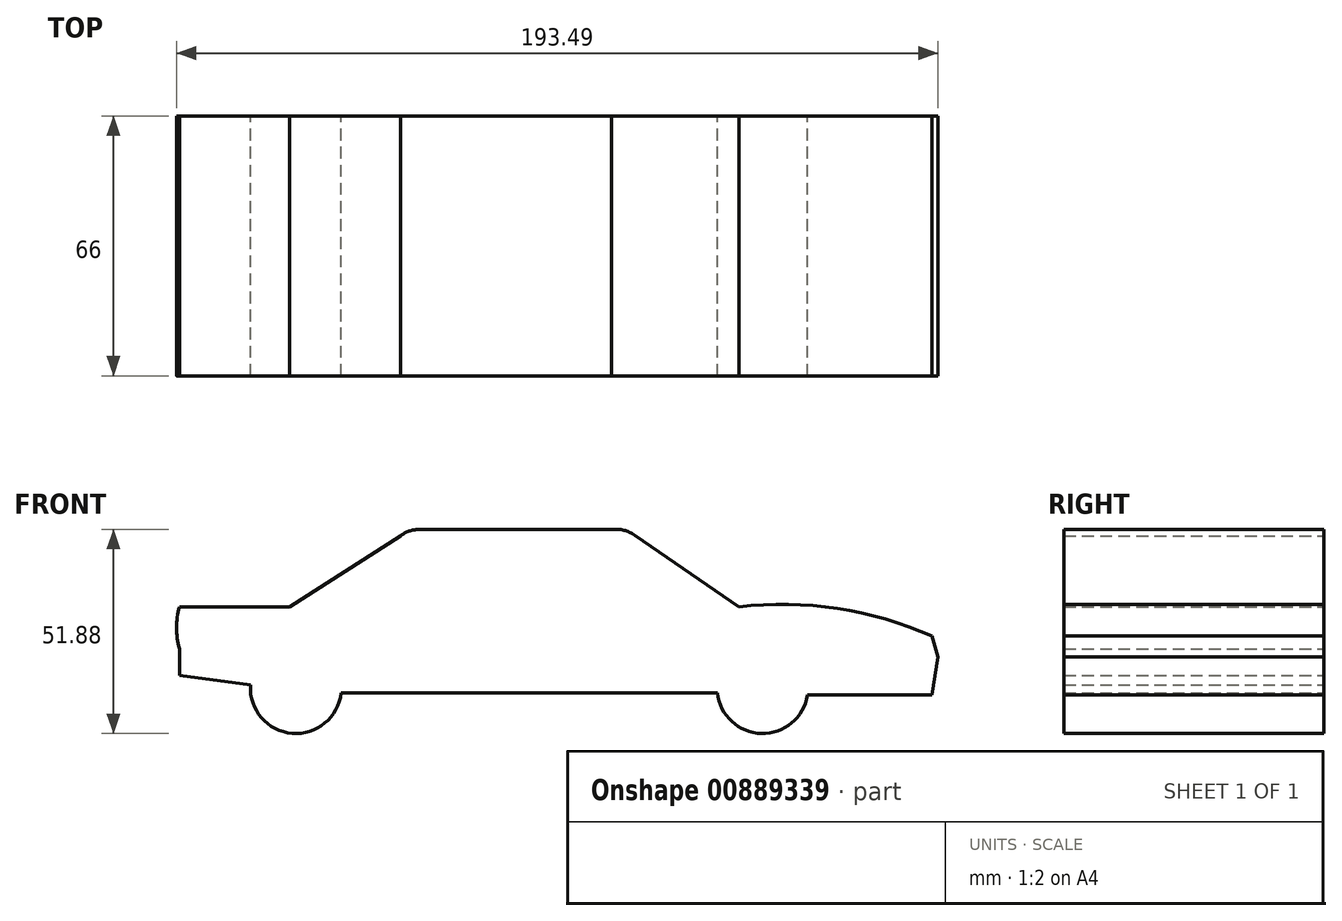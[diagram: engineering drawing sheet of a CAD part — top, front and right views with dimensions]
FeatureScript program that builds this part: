
annotation { "Feature Type Name" : "Feature", "Feature Type Description" : "" }
export const myFeature = defineFeature(function(context is Context, id is Id, definition is map)
    precondition{}
    {
        {
            var Q0;
            Q0=qCreatedBy(makeId("Front.planeOp"),FACE);
            var sketch = newSketch(context, id + "F0", { "sketchPlane" : qUnion([Q0])});
            skLineSegment(sketch, "E0", {"start": v(53.25, 0) * mm, "end": v(26.83, 18.18) * mm});
            skArc(sketch, "E1", {"start": v(26.83, 18.18) * mm, "mid": v(24.03, 19.44) * mm, "end": v(20.96, 19.64) * mm});
            skLineSegment(sketch, "E2", {"start": v(20.96, 19.64) * mm, "end": v(-28.12, 19.64) * mm});
            skArc(sketch, "E3", {"start": v(-28.12, 19.64) * mm, "mid": v(-30.54, 19.22) * mm, "end": v(-32.68, 18.01) * mm});
            skLineSegment(sketch, "E4", {"start": v(-32.68, 18.01) * mm, "end": v(-60.9, 0) * mm});
            skArc(sketch, "E5", {"start": v(102.33, -7.44) * mm, "mid": v(78.29, -0.44) * mm, "end": v(53.25, 0) * mm});
            skLineSegment(sketch, "E6", {"start": v(102.33, -7.44) * mm, "end": v(103.86, -12.72) * mm});
            skLineSegment(sketch, "E7", {"start": v(103.86, -12.72) * mm, "end": v(102.33, -22.43) * mm});
            skCircle(sketch, "E8", {"center": v(59.28, -20.63) * mm, "radius": 11.54 * mm});
            skLineSegment(sketch, "E9", {"start": v(102.33, -22.43) * mm, "end": v(70.69, -22.43) * mm});
            skLineSegment(sketch, "E10", {"start": v(-60.9, 0) * mm, "end": v(-88.84, 0) * mm});
            skLineSegment(sketch, "E11", {"start": v(47.8, -21.87) * mm, "end": v(-47.8, -21.87) * mm});
            skCircle(sketch, "E12.MirrorC", {"center": v(-59.28, -20.63) * mm, "radius": 11.54 * mm});
            skArc(sketch, "E13", {"start": v(-88.84, 0) * mm, "mid": v(-89.63, -5.32) * mm, "end": v(-88.84, -10.64) * mm});
            skLineSegment(sketch, "E14", {"start": v(-88.84, -10.64) * mm, "end": v(-88.84, -17.42) * mm});
            skLineSegment(sketch, "E15", {"start": v(-88.84, -17.42) * mm, "end": v(-70.8, -19.9) * mm});
            skLineSegment(sketch, "E16", {"start": v(53.25, 0) * mm, "end": v(-60.9, 0) * mm});
            skLineSegment(sketch, "E17", {"start": v(53.25, 0) * mm, "end": v(40.88, -12.43) * mm});
            skArc(sketch, "E18", {"start": v(37.13, -21.87) * mm, "mid": v(39.91, -17.51) * mm, "end": v(40.88, -12.43) * mm});
            skLineSegment(sketch, "E19", {"start": v(0, 19.64) * mm, "end": v(0, -21.87) * mm});
            skLineSegment(sketch, "E20", {"start": v(-34.45, 0) * mm, "end": v(-30.54, -21.87) * mm});
            skSolve(sketch);
        }
        {
            var Q0;
            Q0 = qSketchRegion(id + "F0", true);
            extrude(context, id + "F1", {"entities" : qUnion([Q0]), "depth" : 33 * mm, "offsetDistance" : 25 * mm});
        }
        {
            var Q0;
            Q0=makeQuery(id+"F1.opExtrude","SWEPT_BODY",BODY,{"disambiguationData":[OSD([sQuery(id+"F0.wireOp",EDGE,"E0"),sQuery(id+"F0.wireOp",EDGE,"E1"),sQuery(id+"F0.wireOp",EDGE,"E2"),sQuery(id+"F0.wireOp",EDGE,"E3"),sQuery(id+"F0.wireOp",EDGE,"E4"),sQuery(id+"F0.wireOp",EDGE,"E5"),sQuery(id+"F0.wireOp",EDGE,"E6"),sQuery(id+"F0.wireOp",EDGE,"E7"),sQuery(id+"F0.wireOp",EDGE,"E8"),sQuery(id+"F0.wireOp",EDGE,"E9"),sQuery(id+"F0.wireOp",EDGE,"E10"),sQuery(id+"F0.wireOp",EDGE,"E11"),sQuery(id+"F0.wireOp",EDGE,"E12.MirrorC"),sQuery(id+"F0.wireOp",EDGE,"E13"),sQuery(id+"F0.wireOp",EDGE,"E14"),sQuery(id+"F0.wireOp",EDGE,"E15")])]});
            var Q1;
            Q1=qCreatedBy(makeId("Front.planeOp"),FACE);
            mirror(context, id + "F2", {"operationType" : NewBodyOperationType.ADD, "entities" : qUnion([Q0]), "mirrorPlane" : qUnion([Q1])});
        }
    });
